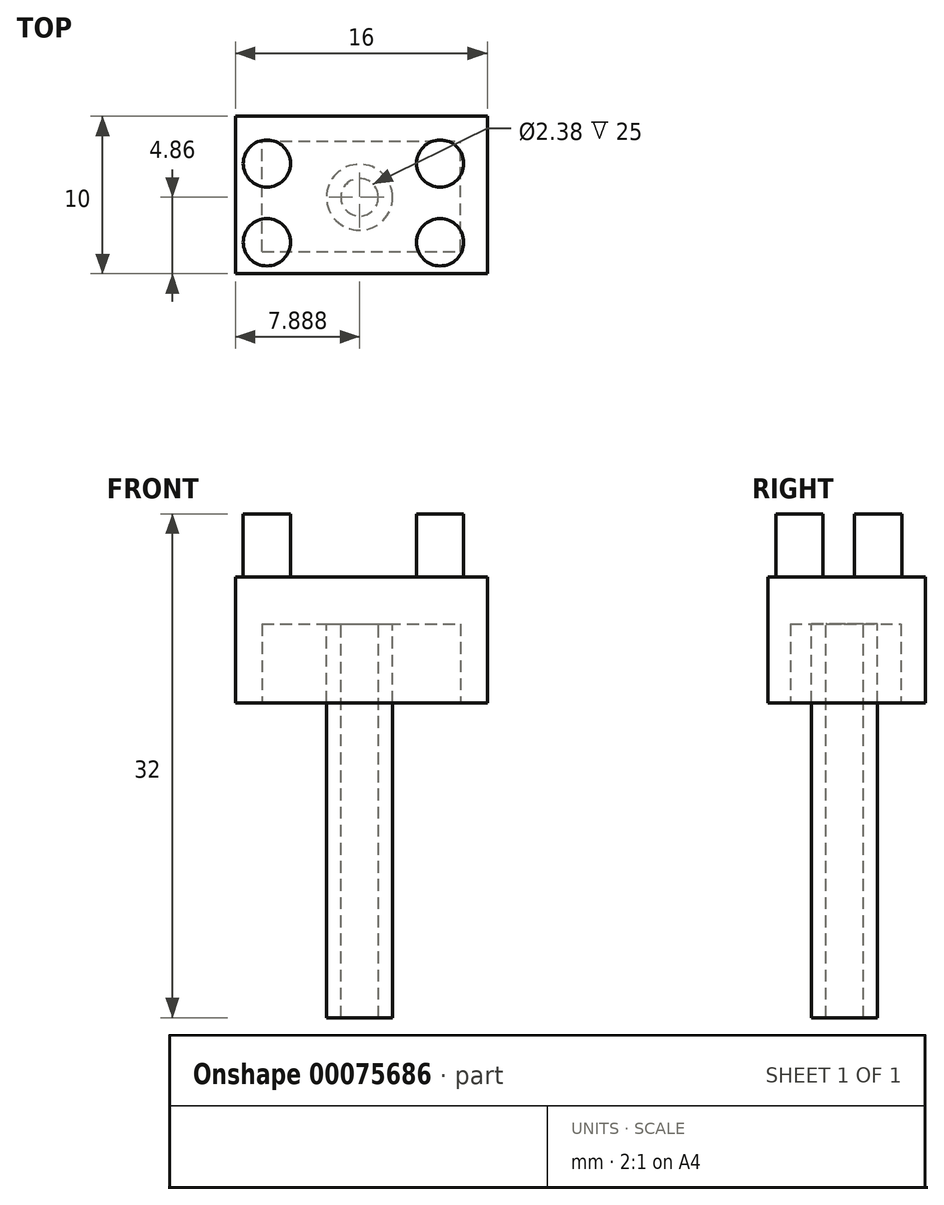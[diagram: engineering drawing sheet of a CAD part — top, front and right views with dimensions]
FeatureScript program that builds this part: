
annotation { "Feature Type Name" : "Feature", "Feature Type Description" : "" }
export const myFeature = defineFeature(function(context is Context, id is Id, definition is map)
    precondition{}
    {
        {
            var Q0;
            Q0=qCreatedBy(makeId("Top.planeOp"),FACE);
            var sketch = newSketch(context, id + "F0", { "sketchPlane" : qUnion([Q0])});
            skLineSegment(sketch, "E0.bottom", {"start": v(0, 0) * mm, "end": v(16, 0) * mm});
            skLineSegment(sketch, "E0.top", {"start": v(0, 10) * mm, "end": v(16, 10) * mm});
            skLineSegment(sketch, "E0.left", {"start": v(0, 0) * mm, "end": v(0, 10) * mm});
            skLineSegment(sketch, "E0.right", {"start": v(16, 0) * mm, "end": v(16, 10) * mm});
            skSolve(sketch);
        }
        {
            var Q0;
            Q0=makeQuery(id+"F0.imprint","IMPRINT",FACE,{"disambiguationData":[TD([[makeQuery(id+"F0.imprint","IMPRINT",EDGE,{"derivedFrom":sQuery(id+"F0.wireOp",EDGE,"E0.bottom")}),1.0]])]});
            extrude(context, id + "F1", {"entities" : qUnion([Q0]), "depth" : 8 * mm});
        }
        {
            var Q0;
            Q0=makeQuery(id+"F1.opExtrude","CAP_FACE",FACE,{"disambiguationData":[OSD([sQuery(id+"F0.wireOp",EDGE,"E0.bottom"),sQuery(id+"F0.wireOp",EDGE,"E0.top"),sQuery(id+"F0.wireOp",EDGE,"E0.left"),sQuery(id+"F0.wireOp",EDGE,"E0.right")])],"isStart":false});
            var sketch = newSketch(context, id + "F2", { "sketchPlane" : qUnion([Q0])});
            skCircle(sketch, "E1", {"center": v(2, 2) * mm, "radius": 1.5 * mm});
            skCircle(sketch, "E2", {"center": v(13, 2) * mm, "radius": 1.5 * mm});
            skLineSegment(sketch, "E3.bottom", {"start": v(2, 2) * mm, "end": v(13, 2) * mm, "construction": true});
            skLineSegment(sketch, "E3.top", {"start": v(2, 7) * mm, "end": v(13, 7) * mm, "construction": true});
            skLineSegment(sketch, "E3.left", {"start": v(2, 2) * mm, "end": v(2, 7) * mm, "construction": true});
            skLineSegment(sketch, "E3.right", {"start": v(13, 2) * mm, "end": v(13, 7) * mm, "construction": true});
            skCircle(sketch, "E4", {"center": v(13, 7) * mm, "radius": 1.5 * mm});
            skCircle(sketch, "E5", {"center": v(2, 7) * mm, "radius": 1.5 * mm});
            skSolve(sketch);
        }
        {
            var Q0;
            Q0 = qSketchRegion(id + "F2", true);
            extrude(context, id + "F3", {"entities" : qUnion([Q0]), "operationType" : NewBodyOperationType.ADD, "depth" : 4 * mm});
        }
        {
            var Q0;
            Q0=makeQuery(id+"F1.opExtrude","CAP_FACE",FACE,{"disambiguationData":[OSD([sQuery(id+"F0.wireOp",EDGE,"E0.bottom"),sQuery(id+"F0.wireOp",EDGE,"E0.top"),sQuery(id+"F0.wireOp",EDGE,"E0.left"),sQuery(id+"F0.wireOp",EDGE,"E0.right")])],"isStart":true});
            var sketch = newSketch(context, id + "F4", { "sketchPlane" : qUnion([Q0])});
            skLineSegment(sketch, "E6.bottom", {"start": v(1.7, -1.42) * mm, "end": v(14.3, -1.42) * mm});
            skLineSegment(sketch, "E6.top", {"start": v(1.7, -8.43) * mm, "end": v(14.3, -8.43) * mm});
            skLineSegment(sketch, "E6.left", {"start": v(1.7, -1.42) * mm, "end": v(1.7, -8.43) * mm});
            skLineSegment(sketch, "E6.right", {"start": v(14.3, -1.42) * mm, "end": v(14.3, -8.43) * mm});
            skSolve(sketch);
        }
        {
            var Q0;
            Q0 = qSketchRegion(id + "F4", true);
            var Q1;
            Q1=makeQuery(id+"F1.opExtrude","CAP_FACE",FACE,{"disambiguationData":[OSD([sQuery(id+"F0.wireOp",EDGE,"E0.bottom"),sQuery(id+"F0.wireOp",EDGE,"E0.top"),sQuery(id+"F0.wireOp",EDGE,"E0.left"),sQuery(id+"F0.wireOp",EDGE,"E0.right")])],"isStart":false});
            extrude(context, id + "F5", {"entities" : qUnion([Q0]), "operationType" : NewBodyOperationType.REMOVE, "oppositeDirection" : true, "endBoundEntityFace" : qUnion([Q1]), "depth" : 5 * mm});
        }
        {
            var Q0;
            Q0=makeQuery(id+"F5.boolean.opBoolean","COPY",FACE,{"derivedFrom":makeQuery(id+"F5.opExtrude","CAP_FACE",FACE,{"disambiguationData":[OSD([sQuery(id+"F4.wireOp",EDGE,"E6.bottom"),sQuery(id+"F4.wireOp",EDGE,"E6.top"),sQuery(id+"F4.wireOp",EDGE,"E6.left"),sQuery(id+"F4.wireOp",EDGE,"E6.right")])],"isStart":false})});
            var sketch = newSketch(context, id + "F6", { "sketchPlane" : qUnion([Q0])});
            skCircle(sketch, "E7", {"center": v(7.89, -4.86) * mm, "radius": 2.1 * mm});
            skCircle(sketch, "E8", {"center": v(7.89, -4.86) * mm, "radius": 1.2 * mm});
            skSolve(sketch);
        }
        {
            var Q0;
            Q0 = qSketchRegion(id + "F6", true);
            extrude(context, id + "F7", {"entities" : qUnion([Q0]), "operationType" : NewBodyOperationType.ADD, "depth" : 25 * mm});
        }
    });
